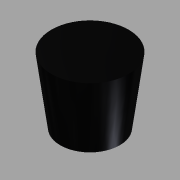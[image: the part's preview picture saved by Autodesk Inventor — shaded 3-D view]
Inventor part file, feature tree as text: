
AUTODESK INVENTOR PART (.ipt)
format: ipt  version: 2014 (Build 180170000, 170)  size: 89,600 bytes
history: native  units: mm
features: sketch x3, plane x1, loft x1, extrude x1
ambient origin geometry x8: Origin, YZ Plane, XZ Plane, XY Plane, X Axis, Y Axis, Z Axis, Center Point
bodies: Solid1 (feature_tree)
feature tree (6):
  sketch  "Sketch1"  dims[d0=27.0mm d1=30.0mm]
  plane  "Work Plane1"
  loft  "Loft1"
  extrude  "Extrusion1"  TaperAngle=0.0deg  [1 undecoded]
  sketch  "Sketch2"  dims[d2=35.0mm d3=0.0mm d4=90.0deg]
  sketch  "Sketch3"  dims[d5=0.0mm d6=90.0deg d7=25.5mm d8=28.0mm d9=0.0mm]
note: 1 required parameter value undecoded (feature->parameter linkage not recoverable at this tier; creation-order binding heuristic only, values carry confidence <= 0.55)
